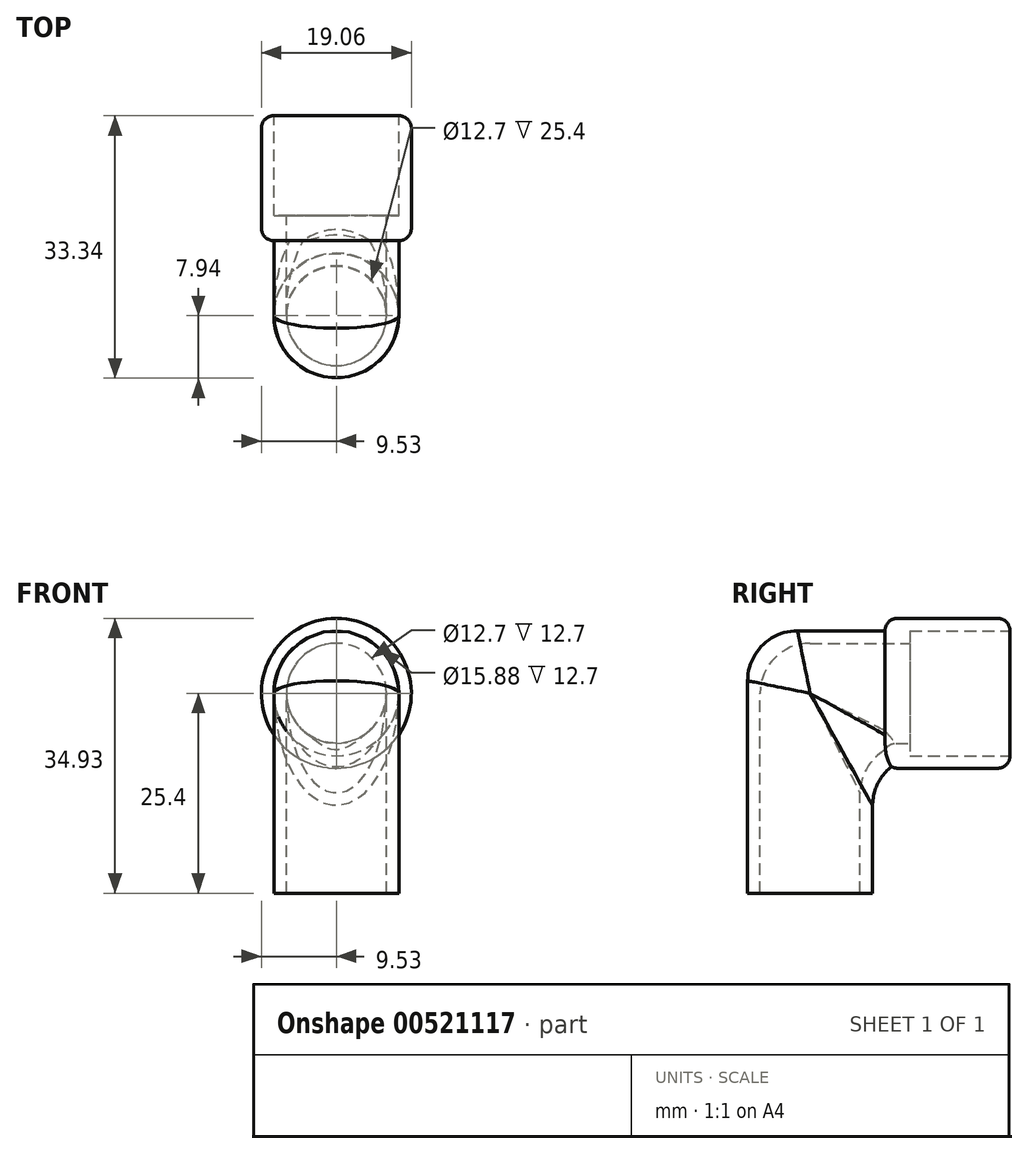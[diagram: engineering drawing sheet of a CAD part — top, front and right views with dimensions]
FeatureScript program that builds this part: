
annotation { "Feature Type Name" : "Feature", "Feature Type Description" : "" }
export const myFeature = defineFeature(function(context is Context, id is Id, definition is map)
    precondition{}
    {
        {
            var Q0;
            Q0=qCreatedBy(makeId("Top.planeOp"),FACE);
            var sketch = newSketch(context, id + "F0", { "sketchPlane" : qUnion([Q0])});
            skCircle(sketch, "E0", {"center": v(0, 0) * mm, "radius": 6.35 * mm});
            skCircle(sketch, "E1", {"center": v(0, 0) * mm, "radius": 7.94 * mm});
            skSolve(sketch);
        }
        {
            var Q0;
            Q0=qCreatedBy(makeId("Right.planeOp"),FACE);
            var sketch = newSketch(context, id + "F1", { "sketchPlane" : qUnion([Q0])});
            skLineSegment(sketch, "E2", {"start": v(0, 0) * mm, "end": v(0, 25.4) * mm});
            skLineSegment(sketch, "E3", {"start": v(25.4, 25.4) * mm, "end": v(0, 25.4) * mm});
            skSolve(sketch);
        }
        {
            var Q0;
            Q0=makeQuery(id+"F0.imprint","IMPRINT",FACE,{"disambiguationData":[TD([[makeQuery(id+"F0.imprint","IMPRINT",EDGE,{"derivedFrom":sQuery(id+"F0.wireOp",EDGE,"E0")}),-1.0]])]});
            var Q1;
            Q1=sQuery(id+"F1.wireOp",EDGE,"E3");
            var Q2;
            Q2=sQuery(id+"F1.wireOp",EDGE,"E2");
            sweep(context, id + "F2", {"profiles" : qUnion([Q0]), "path" : qUnion([Q1, Q2])});
        }
        {
            var Q0;
            Q0=makeQuery(id+"F2.opSweep","MID_CAP_EDGE",EDGE,{"disambiguationData":[OSD([sQuery(id+"F0.wireOp",EDGE,"E1"),sQuery(id+"F1.wireOp",VERTEX,"E2.end")])],"capPos":1.0});
            var Q1;
            Q1=makeQuery(id+"F2.opSweep","MID_CAP_EDGE",EDGE,{"disambiguationData":[OSD([sQuery(id+"F0.wireOp",EDGE,"E0"),sQuery(id+"F1.wireOp",VERTEX,"E2.end")])],"capPos":1.0});
            fillet(context, id + "F3", {"entities" : qUnion([Q0, Q1]), "radius" : 6.35 * mm, "tangentPropagation" : true, "allowEdgeOverflow" : false});
        }
        {
            var Q0;
            Q0=makeQuery(id+"F2.opSweep","CAP_FACE",FACE,{"disambiguationData":[OSD([sQuery(id+"F0.wireOp",EDGE,"E0"),sQuery(id+"F0.wireOp",EDGE,"E1"),sQuery(id+"F1.wireOp",VERTEX,"E3.start")])],"isStart":false});
            var sketch = newSketch(context, id + "F4", { "sketchPlane" : qUnion([Q0])});
            skCircle(sketch, "E4", {"center": v(0, 25.4) * mm, "radius": 9.53 * mm});
            skSolve(sketch);
        }
        {
            var Q0;
            Q0 = qSketchRegion(id + "F4", true);
            extrude(context, id + "F5", {"entities" : qUnion([Q0]), "operationType" : NewBodyOperationType.ADD, "oppositeDirection" : true, "depth" : 15.88 * mm, "offsetDistance" : 25.4 * mm});
        }
        {
            var Q0;
            {var subQ0=sQuery(id+"F1.wireOp",VERTEX,"E3.start");var subQ1=sQuery(id+"F0.wireOp",EDGE,"E1");Q0=makeQuery(id+"F4uz0T4iYYrPmTx_1.boolean.opBoolean","MERGE",FACE,{"derivedFrom":[makeQuery(id+"F2.opSweep","CAP_FACE",FACE,{"disambiguationData":[OSD([sQuery(id+"F0.wireOp",EDGE,"E0"),subQ1,subQ0])],"isStart":false}),makeQuery(id+"F4uz0T4iYYrPmTx_1.opExtrude","CAP_FACE",FACE,{"disambiguationData":[OSD([subQ1,subQ0,sQuery(id+"F4.wireOp",EDGE,"E4")])],"isStart":true})]});}
            var sketch = newSketch(context, id + "F6", { "sketchPlane" : qUnion([Q0])});
            skCircle(sketch, "E5", {"center": v(0, 25.4) * mm, "radius": 7.94 * mm});
            skSolve(sketch);
        }
        {
            var Q0;
            Q0 = qSketchRegion(id + "F6", true);
            extrude(context, id + "F7", {"entities" : qUnion([Q0]), "operationType" : NewBodyOperationType.REMOVE, "oppositeDirection" : true, "depth" : 12.7 * mm, "offsetDistance" : 25.4 * mm});
        }
        {
            var Q0;
            Q0=makeQuery(id+"F7.boolean.opBoolean","COPY",FACE,{"derivedFrom":makeQuery(id+"F7.opExtrude","CAP_FACE",FACE,{"disambiguationData":[OSD([sQuery(id+"F6.wireOp",EDGE,"E5")])],"isStart":false})});
            var sketch = newSketch(context, id + "F8", { "sketchPlane" : qUnion([Q0])});
            skCircle(sketch, "E6", {"center": v(0, 25.4) * mm, "radius": 6.35 * mm});
            skSolve(sketch);
        }
        {
            var Q0;
            Q0 = qSketchRegion(id + "F8", true);
            extrude(context, id + "F9", {"entities" : qUnion([Q0]), "operationType" : NewBodyOperationType.REMOVE, "oppositeDirection" : true, "depth" : 4.14 * mm, "offsetDistance" : 25.4 * mm});
        }
        {
            var Q0;
            Q0=makeQuery(id+"F9.boolean.opBoolean","COPY",EDGE,{"derivedFrom":makeQuery(id+"F9.opExtrude","CAP_EDGE",EDGE,{"disambiguationData":[OSD([sQuery(id+"F8.wireOp",EDGE,"E6")])],"isStart":true})});
            var Q1;
            Q1=makeQuery(id+"F5.opExtrude","CAP_EDGE",EDGE,{"disambiguationData":[OSD([sQuery(id+"F4.wireOp",EDGE,"E4")])],"isStart":true});
            var Q2;
            {var subQ0=sQuery(id+"F0.wireOp",EDGE,"E0");Q2=makeQuery(id+"F9.boolean.opBoolean","INTERSECT",EDGE,{"derivedFrom":[makeQuery(id+"F5.boolean.opBoolean","SPLIT",FACE,{"disambiguationData":[TD([makeQuery(id+"F2.opSweep","SWEPT_FACE",FACE,{"disambiguationData":[OSD([subQ0,sQuery(id+"F1.wireOp",EDGE,"E3")])]})])],"derivedFrom":makeQuery(id+"F5.opExtrude","CAP_FACE",FACE,{"disambiguationData":[OSD([sQuery(id+"F4.wireOp",EDGE,"E4")])],"isStart":false})}),makeQuery(id+"F9.opExtrude","SWEPT_FACE",FACE,{"disambiguationData":[OSD([sQuery(id+"F8.wireOp",EDGE,"E6")])]})]});}
            var Q3;
            Q3=makeQuery(id+"F5.opExtrude","CAP_EDGE",EDGE,{"disambiguationData":[OSD([sQuery(id+"F4.wireOp",EDGE,"E4")])],"isStart":false});
            fillet(context, id + "F10", {"entities" : qUnion([Q0, Q1, Q2, Q3]), "radius" : 1.59 * mm, "tangentPropagation" : true, "allowEdgeOverflow" : false});
        }
    });
